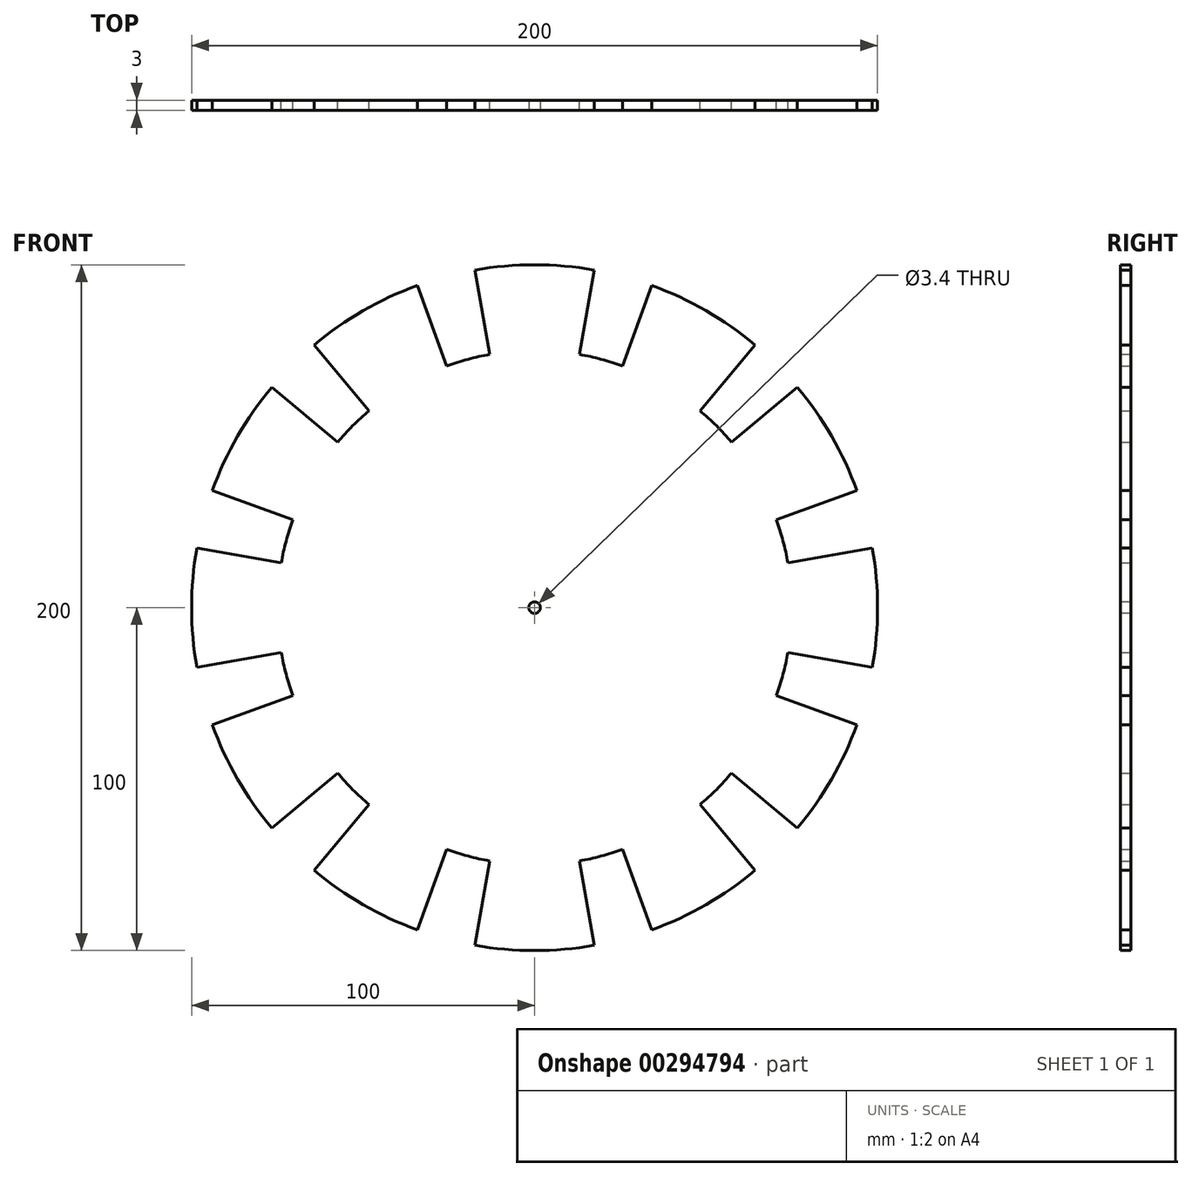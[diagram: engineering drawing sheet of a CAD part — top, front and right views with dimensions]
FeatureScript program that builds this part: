
annotation { "Feature Type Name" : "Feature", "Feature Type Description" : "" }
export const myFeature = defineFeature(function(context is Context, id is Id, definition is map)
    precondition{}
    {
        {
            var Q0;
            Q0=qCreatedBy(makeId("Front.planeOp"),FACE);
            var sketch = newSketch(context, id + "F0", { "sketchPlane" : qUnion([Q0])});
            skCircle(sketch, "E0", {"center": v(0, 0) * mm, "radius": 75 * mm});
            skArc(sketch, "E1", {"start": v(-34.2, 93.97) * mm, "mid": v(-50, 86.6) * mm, "end": v(-64.28, 76.6) * mm});
            skLineSegment(sketch, "E2", {"start": v(0, 100) * mm, "end": v(0, -100) * mm});
            skLineSegment(sketch, "E3", {"start": v(-100, 0) * mm, "end": v(100, 0) * mm});
            skLineSegment(sketch, "E4", {"start": v(0, 0) * mm, "end": v(50, 86.6) * mm});
            skLineSegment(sketch, "E5", {"start": v(0, 0) * mm, "end": v(86.6, 50) * mm});
            skLineSegment(sketch, "E6", {"start": v(0, 0) * mm, "end": v(86.6, -50) * mm});
            skLineSegment(sketch, "E7", {"start": v(0, 0) * mm, "end": v(50, -86.6) * mm});
            skLineSegment(sketch, "E8", {"start": v(0, 0) * mm, "end": v(-50, 86.6) * mm});
            skLineSegment(sketch, "E9", {"start": v(0, 0) * mm, "end": v(-86.6, 50) * mm});
            skLineSegment(sketch, "E10", {"start": v(0, 0) * mm, "end": v(-86.6, -50) * mm});
            skLineSegment(sketch, "E11", {"start": v(0, 0) * mm, "end": v(-50, -86.6) * mm});
            skLineSegment(sketch, "E12", {"start": v(0, 0) * mm, "end": v(-17.36, 98.48) * mm});
            skLineSegment(sketch, "E13", {"start": v(17.36, 98.48) * mm, "end": v(0, 0) * mm});
            skLineSegment(sketch, "E14", {"start": v(0, 0) * mm, "end": v(34.2, 93.97) * mm});
            skLineSegment(sketch, "E15", {"start": v(64.28, 76.6) * mm, "end": v(0, 0) * mm});
            skLineSegment(sketch, "E16", {"start": v(0, 0) * mm, "end": v(76.6, 64.28) * mm});
            skLineSegment(sketch, "E17", {"start": v(93.97, 34.2) * mm, "end": v(0, 0) * mm});
            skLineSegment(sketch, "E18", {"start": v(0, 0) * mm, "end": v(98.48, 17.36) * mm});
            skLineSegment(sketch, "E19", {"start": v(0, 0) * mm, "end": v(93.97, -34.2) * mm});
            skLineSegment(sketch, "E20", {"start": v(76.6, -64.28) * mm, "end": v(0, 0) * mm});
            skLineSegment(sketch, "E21", {"start": v(0, 0) * mm, "end": v(98.48, -17.36) * mm});
            skLineSegment(sketch, "E22", {"start": v(0, 0) * mm, "end": v(64.28, -76.6) * mm});
            skLineSegment(sketch, "E23", {"start": v(34.2, -93.97) * mm, "end": v(0, 0) * mm});
            skLineSegment(sketch, "E24", {"start": v(0, 0) * mm, "end": v(17.36, -98.48) * mm});
            skLineSegment(sketch, "E25", {"start": v(-17.36, -98.48) * mm, "end": v(0, 0) * mm});
            skLineSegment(sketch, "E26", {"start": v(0, 0) * mm, "end": v(-34.2, -93.97) * mm});
            skLineSegment(sketch, "E27", {"start": v(-64.28, -76.6) * mm, "end": v(0, 0) * mm});
            skLineSegment(sketch, "E28", {"start": v(0, 0) * mm, "end": v(-76.6, -64.28) * mm});
            skLineSegment(sketch, "E29", {"start": v(-93.97, -34.2) * mm, "end": v(0, 0) * mm});
            skLineSegment(sketch, "E30", {"start": v(0, 0) * mm, "end": v(-98.48, -17.36) * mm});
            skLineSegment(sketch, "E31", {"start": v(0, 0) * mm, "end": v(-93.97, 34.2) * mm});
            skLineSegment(sketch, "E32", {"start": v(-76.6, 64.28) * mm, "end": v(0, 0) * mm});
            skLineSegment(sketch, "E33", {"start": v(0, 0) * mm, "end": v(-64.28, 76.6) * mm});
            skLineSegment(sketch, "E34", {"start": v(-34.2, 93.97) * mm, "end": v(0, 0) * mm});
            skArc(sketch, "E35.trimOffspring", {"start": v(17.36, 98.48) * mm, "mid": v(0, 100) * mm, "end": v(-17.36, 98.48) * mm});
            skArc(sketch, "E36.trimOffspring", {"start": v(64.28, 76.6) * mm, "mid": v(50, 86.6) * mm, "end": v(34.2, 93.97) * mm});
            skArc(sketch, "E37.trimOffspring", {"start": v(93.97, 34.2) * mm, "mid": v(86.6, 50) * mm, "end": v(76.6, 64.28) * mm});
            skArc(sketch, "E38.trimOffspring", {"start": v(98.48, -17.36) * mm, "mid": v(100, 0) * mm, "end": v(98.48, 17.36) * mm});
            skArc(sketch, "E39.trimOffspring", {"start": v(76.6, -64.28) * mm, "mid": v(86.6, -50) * mm, "end": v(93.97, -34.2) * mm});
            skArc(sketch, "E40.trimOffspring", {"start": v(34.2, -93.97) * mm, "mid": v(50, -86.6) * mm, "end": v(64.28, -76.6) * mm});
            skArc(sketch, "E41.trimOffspring", {"start": v(-17.36, -98.48) * mm, "mid": v(0, -100) * mm, "end": v(17.36, -98.48) * mm});
            skArc(sketch, "E42.trimOffspring", {"start": v(-64.28, -76.6) * mm, "mid": v(-50, -86.6) * mm, "end": v(-34.2, -93.97) * mm});
            skArc(sketch, "E43.trimOffspring", {"start": v(-93.97, -34.2) * mm, "mid": v(-86.6, -50) * mm, "end": v(-76.6, -64.28) * mm});
            skArc(sketch, "E44.trimOffspring", {"start": v(-98.48, 17.36) * mm, "mid": v(-100, 0) * mm, "end": v(-98.48, -17.36) * mm});
            skArc(sketch, "E45.trimOffspring", {"start": v(-76.6, 64.28) * mm, "mid": v(-86.6, 50) * mm, "end": v(-93.97, 34.2) * mm});
            skLineSegment(sketch, "E46", {"start": v(-98.48, 17.36) * mm, "end": v(0, 0) * mm});
            skSolve(sketch);
        }
        {
            var Q0;
            Q0 = qSketchRegion(id + "F0", true);
            extrude(context, id + "F1", {"entities" : qUnion([Q0]), "depth" : 3 * mm});
        }
        {
            var Q0;
            Q0=makeQuery(id+"F1.opExtrude","CAP_FACE",FACE,{"disambiguationData":[OSD([sQuery(id+"F0.wireOp",EDGE,"E0"),sQuery(id+"F0.wireOp",EDGE,"E1"),sQuery(id+"F0.wireOp",EDGE,"E12"),sQuery(id+"F0.wireOp",EDGE,"E13"),sQuery(id+"F0.wireOp",EDGE,"E14"),sQuery(id+"F0.wireOp",EDGE,"E15"),sQuery(id+"F0.wireOp",EDGE,"E16"),sQuery(id+"F0.wireOp",EDGE,"E17"),sQuery(id+"F0.wireOp",EDGE,"E18"),sQuery(id+"F0.wireOp",EDGE,"E19"),sQuery(id+"F0.wireOp",EDGE,"E20"),sQuery(id+"F0.wireOp",EDGE,"E21"),sQuery(id+"F0.wireOp",EDGE,"E22"),sQuery(id+"F0.wireOp",EDGE,"E23"),sQuery(id+"F0.wireOp",EDGE,"E24"),sQuery(id+"F0.wireOp",EDGE,"E25"),sQuery(id+"F0.wireOp",EDGE,"E26"),sQuery(id+"F0.wireOp",EDGE,"E27"),sQuery(id+"F0.wireOp",EDGE,"E28"),sQuery(id+"F0.wireOp",EDGE,"E29"),sQuery(id+"F0.wireOp",EDGE,"E30"),sQuery(id+"F0.wireOp",EDGE,"E31"),sQuery(id+"F0.wireOp",EDGE,"E32"),sQuery(id+"F0.wireOp",EDGE,"E33"),sQuery(id+"F0.wireOp",EDGE,"E34"),sQuery(id+"F0.wireOp",EDGE,"E35.trimOffspring"),sQuery(id+"F0.wireOp",EDGE,"E36.trimOffspring"),sQuery(id+"F0.wireOp",EDGE,"E37.trimOffspring"),sQuery(id+"F0.wireOp",EDGE,"E38.trimOffspring"),sQuery(id+"F0.wireOp",EDGE,"E39.trimOffspring"),sQuery(id+"F0.wireOp",EDGE,"E40.trimOffspring"),sQuery(id+"F0.wireOp",EDGE,"E41.trimOffspring"),sQuery(id+"F0.wireOp",EDGE,"E42.trimOffspring"),sQuery(id+"F0.wireOp",EDGE,"E43.trimOffspring"),sQuery(id+"F0.wireOp",EDGE,"E44.trimOffspring"),sQuery(id+"F0.wireOp",EDGE,"E45.trimOffspring"),sQuery(id+"F0.wireOp",EDGE,"E46")])],"isStart":false});
            var sketch = newSketch(context, id + "F2", { "sketchPlane" : qUnion([Q0])});
            skCircle(sketch, "E47", {"center": v(0, 0) * mm, "radius": 1.7 * mm});
            skSolve(sketch);
        }
        {
            var Q0;
            Q0 = qSketchRegion(id + "F2", true);
            extrude(context, id + "F3", {"entities" : qUnion([Q0]), "operationType" : NewBodyOperationType.REMOVE, "endBound" : BoundingType.THROUGH_ALL, "oppositeDirection" : true, "depth" : 25 * mm});
        }
    });
